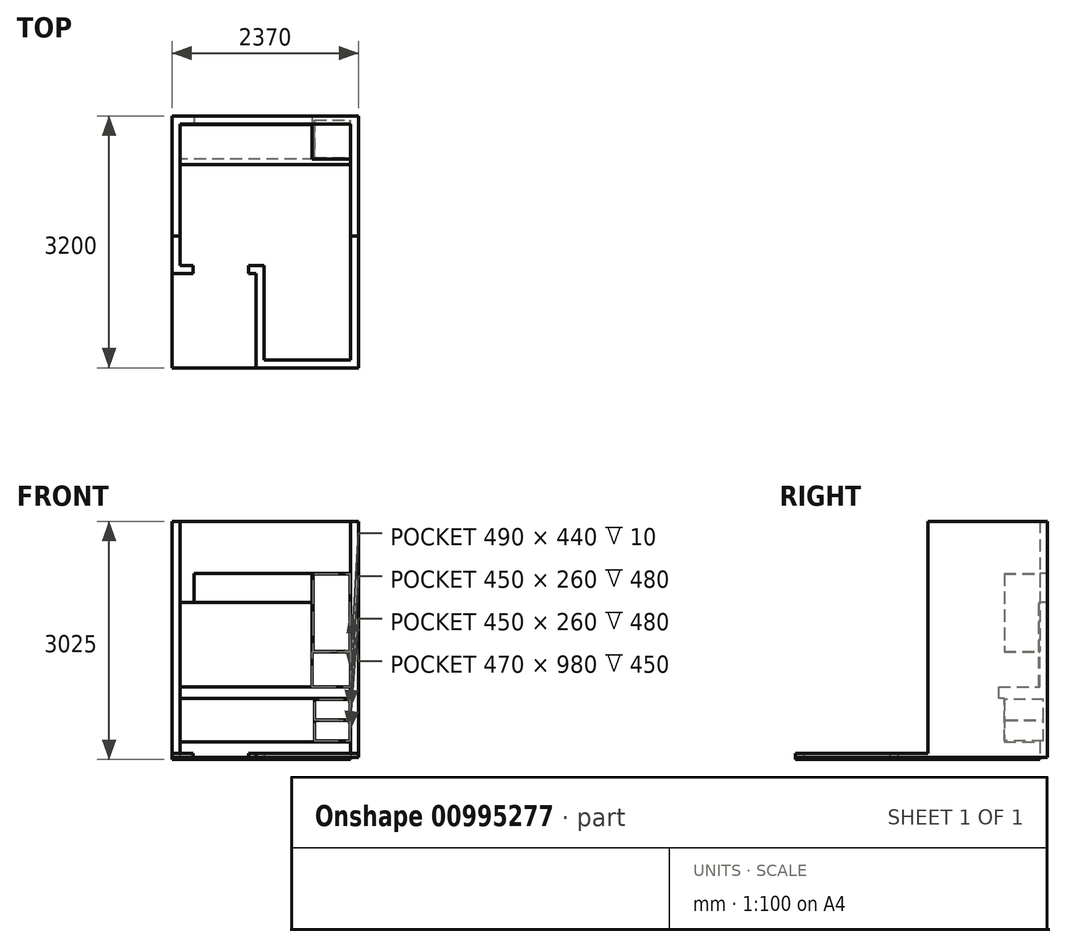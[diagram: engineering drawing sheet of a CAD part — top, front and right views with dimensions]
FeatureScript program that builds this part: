
annotation { "Feature Type Name" : "Feature", "Feature Type Description" : "" }
export const myFeature = defineFeature(function(context is Context, id is Id, definition is map)
    precondition{}
    {
        {
            var Q0;
            Q0=qCreatedBy(makeId("Top.planeOp"),FACE);
            var sketch = newSketch(context, id + "F0", { "sketchPlane" : qUnion([Q0])});
            skLineSegment(sketch, "E0", {"start": v(0, 0) * mm, "end": v(0, 1800) * mm});
            skLineSegment(sketch, "E1", {"start": v(0, 1800) * mm, "end": v(2170, 1800) * mm});
            skLineSegment(sketch, "E2", {"start": v(2170, 1800) * mm, "end": v(2170, -1200) * mm});
            skLineSegment(sketch, "E3", {"start": v(2170, -1200) * mm, "end": v(1070, -1200) * mm});
            skLineSegment(sketch, "E4", {"start": v(1070, -1200) * mm, "end": v(1070, 0) * mm});
            skLineSegment(sketch, "E5", {"start": v(1070, 0) * mm, "end": v(0, 0) * mm});
            skLineSegment(sketch, "E6.0", {"start": v(-100, 1900) * mm, "end": v(2270, 1900) * mm});
            skLineSegment(sketch, "E7.0", {"start": v(2270, 1900) * mm, "end": v(2270, -1300) * mm});
            skLineSegment(sketch, "E8.0", {"start": v(-100, -100) * mm, "end": v(-100, 1900) * mm});
            skLineSegment(sketch, "E8.1", {"start": v(970, -100) * mm, "end": v(-100, -100) * mm});
            skLineSegment(sketch, "E8.2", {"start": v(970, -1300) * mm, "end": v(970, -100) * mm});
            skLineSegment(sketch, "E8.3", {"start": v(2270, -1300) * mm, "end": v(970, -1300) * mm});
            skSolve(sketch);
        }
        {
            var Q0;
            Q0 = qSketchRegion(id + "F0", true);
            extrude(context, id + "F1", {"entities" : qUnion([Q0]), "depth" : 3000 * mm, "offsetDistance" : 25 * mm});
        }
        {
            var Q0;
            Q0=makeQuery(id+"F1.opExtrude","SWEPT_FACE",FACE,{"disambiguationData":[OSD([sQuery(id+"F0.wireOp",EDGE,"E8.1")])]});
            var sketch = newSketch(context, id + "F2", { "sketchPlane" : qUnion([Q0])});
            skLineSegment(sketch, "E9.bottom", {"start": v(170, 0) * mm, "end": v(870, 0) * mm});
            skLineSegment(sketch, "E9.top", {"start": v(170, 2100) * mm, "end": v(870, 2100) * mm});
            skLineSegment(sketch, "E9.left", {"start": v(170, 0) * mm, "end": v(170, 2100) * mm});
            skLineSegment(sketch, "E9.right", {"start": v(870, 0) * mm, "end": v(870, 2100) * mm});
            skSolve(sketch);
        }
        {
            var Q0;
            Q0=makeQuery(id+"F2.imprint","IMPRINT",FACE,{"disambiguationData":[TD([[makeQuery(id+"F2.imprint","IMPRINT",EDGE,{"derivedFrom":sQuery(id+"F2.wireOp",EDGE,"E9.bottom")}),-1.0]])]});
            extrude(context, id + "F3", {"entities" : qUnion([Q0]), "operationType" : NewBodyOperationType.REMOVE, "endBound" : BoundingType.UP_TO_NEXT, "oppositeDirection" : true, "depth" : 25 * mm, "offsetDistance" : 25 * mm});
        }
        {
            var Q0;
            Q0=makeQuery(id+"F1.opExtrude","SWEPT_FACE",FACE,{"disambiguationData":[OSD([sQuery(id+"F0.wireOp",EDGE,"E1")])]});
            var sketch = newSketch(context, id + "F4", { "sketchPlane" : qUnion([Q0])});
            skLineSegment(sketch, "E10.bottom", {"start": v(180, 2340) * mm, "end": v(1680, 2340) * mm});
            skLineSegment(sketch, "E10.top", {"start": v(180, 1970) * mm, "end": v(1680, 1970) * mm});
            skLineSegment(sketch, "E10.left", {"start": v(180, 2340) * mm, "end": v(180, 1970) * mm});
            skLineSegment(sketch, "E10.right", {"start": v(1680, 2340) * mm, "end": v(1680, 1970) * mm});
            skSolve(sketch);
        }
        {
            var Q0;
            Q0=makeQuery(id+"F4.imprint","IMPRINT",FACE,{"disambiguationData":[TD([[makeQuery(id+"F4.imprint","IMPRINT",EDGE,{"derivedFrom":sQuery(id+"F4.wireOp",EDGE,"E10.bottom")}),-1.0]])]});
            extrude(context, id + "F5", {"entities" : qUnion([Q0]), "operationType" : NewBodyOperationType.REMOVE, "endBound" : BoundingType.UP_TO_NEXT, "oppositeDirection" : true, "depth" : 25 * mm, "offsetDistance" : 25 * mm});
        }
        {
            var Q0;
            Q0=makeQuery(id+"F1.opExtrude","CAP_FACE",FACE,{"disambiguationData":[OSD([sQuery(id+"F0.wireOp",EDGE,"E0"),sQuery(id+"F0.wireOp",EDGE,"E1"),sQuery(id+"F0.wireOp",EDGE,"E2"),sQuery(id+"F0.wireOp",EDGE,"E3"),sQuery(id+"F0.wireOp",EDGE,"E4"),sQuery(id+"F0.wireOp",EDGE,"E5"),sQuery(id+"F0.wireOp",EDGE,"E6.0"),sQuery(id+"F0.wireOp",EDGE,"E7.0"),sQuery(id+"F0.wireOp",EDGE,"E8.0"),sQuery(id+"F0.wireOp",EDGE,"E8.1"),sQuery(id+"F0.wireOp",EDGE,"E8.2"),sQuery(id+"F0.wireOp",EDGE,"E8.3")])],"isStart":true});
            var sketch = newSketch(context, id + "F6", { "sketchPlane" : qUnion([Q0])});
            skLineSegment(sketch, "E11.bottom", {"start": v(-100, -1900) * mm, "end": v(2270, -1900) * mm});
            skLineSegment(sketch, "E11.top", {"start": v(-100, 1300) * mm, "end": v(2270, 1300) * mm});
            skLineSegment(sketch, "E11.left", {"start": v(-100, -1900) * mm, "end": v(-100, 1300) * mm});
            skLineSegment(sketch, "E11.right", {"start": v(2270, -1900) * mm, "end": v(2270, 1300) * mm});
            skSolve(sketch);
        }
        {
            var Q0;
            {var subQ12=sQuery(id+"F0.wireOp",EDGE,"E0");Q0=makeQuery(id+"F6.imprint","IMPRINT",FACE,{"disambiguationData":[TD([[makeQuery(id+"F6.imprint","IMPRINT",EDGE,{"derivedFrom":makeQuery(id+"F1.opExtrude","CAP_EDGE",EDGE,{"disambiguationData":[OSD([subQ12])],"isStart":true})}),1.0]])]});}
            extrude(context, id + "F7", {"entities" : qUnion([Q0]), "depth" : 25 * mm, "offsetDistance" : 25 * mm});
        }
        {
            var Q0;
            Q0=makeQuery(id+"F1.opExtrude","CAP_FACE",FACE,{"disambiguationData":[OSD([sQuery(id+"F0.wireOp",EDGE,"E0"),sQuery(id+"F0.wireOp",EDGE,"E1"),sQuery(id+"F0.wireOp",EDGE,"E2"),sQuery(id+"F0.wireOp",EDGE,"E3"),sQuery(id+"F0.wireOp",EDGE,"E4"),sQuery(id+"F0.wireOp",EDGE,"E5"),sQuery(id+"F0.wireOp",EDGE,"E6.0"),sQuery(id+"F0.wireOp",EDGE,"E7.0"),sQuery(id+"F0.wireOp",EDGE,"E8.0"),sQuery(id+"F0.wireOp",EDGE,"E8.1"),sQuery(id+"F0.wireOp",EDGE,"E8.2"),sQuery(id+"F0.wireOp",EDGE,"E8.3")])],"isStart":false});
            var sketch = newSketch(context, id + "F8", { "sketchPlane" : qUnion([Q0])});
            skLineSegment(sketch, "E12.bottom", {"start": v(2466.68, -1550.03) * mm, "end": v(-472.08, -1550.03) * mm});
            skLineSegment(sketch, "E12.top", {"start": v(2466.68, 377.63) * mm, "end": v(-472.08, 377.63) * mm});
            skLineSegment(sketch, "E12.left", {"start": v(2466.68, -1550.03) * mm, "end": v(2466.68, 377.63) * mm});
            skLineSegment(sketch, "E12.right", {"start": v(-472.08, -1550.03) * mm, "end": v(-472.08, 377.63) * mm});
            skSolve(sketch);
        }
        {
            var Q0;
            Q0=makeQuery(id+"F8.imprint","IMPRINT",FACE,{"disambiguationData":[TD([[makeQuery(id+"F8.imprint","IMPRINT",EDGE,{"derivedFrom":sQuery(id+"F8.wireOp",EDGE,"E12.bottom")}),-1.0]])]});
            var Q1;
            {var subQ1=makeQuery(id+"F1.opExtrude","CAP_EDGE",EDGE,{"disambiguationData":[OSD([sQuery(id+"F0.wireOp",EDGE,"E3")])],"isStart":false});Q1=makeQuery(id+"F8.imprint","IMPRINT",FACE,{"disambiguationData":[TD([[makeQuery(id+"F8.imprint","IMPRINT",EDGE,{"derivedFrom":subQ1}),-1.0]])]});}
            var Q2;
            {var subQ0=makeQuery(id+"F1.opExtrude","CAP_EDGE",EDGE,{"disambiguationData":[OSD([sQuery(id+"F0.wireOp",EDGE,"E3")])],"isStart":false});Q2=makeQuery(id+"F8.imprint","IMPRINT",FACE,{"disambiguationData":[TD([[makeQuery(id+"F8.imprint","IMPRINT",EDGE,{"derivedFrom":subQ0}),1.0]])]});}
            extrude(context, id + "F9", {"entities" : qUnion([Q0, Q1, Q2]), "operationType" : NewBodyOperationType.REMOVE, "oppositeDirection" : true, "depth" : 2950 * mm, "offsetDistance" : 25 * mm});
        }
        {
            var Q0;
            Q0=makeQuery(id+"F1.opExtrude","SWEPT_FACE",FACE,{"disambiguationData":[OSD([sQuery(id+"F0.wireOp",EDGE,"E1")])]});
            var sketch = newSketch(context, id + "F10", { "sketchPlane" : qUnion([Q0])});
            skLineSegment(sketch, "E13.bottom", {"start": v(2170, 900) * mm, "end": v(0, 900) * mm});
            skLineSegment(sketch, "E13.top", {"start": v(2170, 200) * mm, "end": v(0, 200) * mm});
            skLineSegment(sketch, "E13.left", {"start": v(2170, 900) * mm, "end": v(2170, 200) * mm});
            skLineSegment(sketch, "E13.right", {"start": v(0, 900) * mm, "end": v(0, 200) * mm});
            skSolve(sketch);
        }
        {
            var Q0;
            Q0=makeQuery(id+"F10.imprint","IMPRINT",FACE,{"disambiguationData":[TD([[makeQuery(id+"F10.imprint","IMPRINT",EDGE,{"derivedFrom":sQuery(id+"F10.wireOp",EDGE,"E13.bottom")}),1.0]])]});
            extrude(context, id + "F11", {"entities" : qUnion([Q0]), "operationType" : NewBodyOperationType.ADD, "depth" : 450 * mm, "offsetDistance" : 25 * mm});
        }
        {
            var Q0;
            Q0=makeQuery(id+"F11.opExtrude","SWEPT_FACE",FACE,{"disambiguationData":[OSD([sQuery(id+"F10.wireOp",EDGE,"E13.bottom")])]});
            var sketch = newSketch(context, id + "F12", { "sketchPlane" : qUnion([Q0])});
            skLineSegment(sketch, "E14.bottom", {"start": v(0, 1800) * mm, "end": v(2170, 1800) * mm});
            skLineSegment(sketch, "E14.top", {"start": v(0, 1280) * mm, "end": v(2170, 1280) * mm});
            skLineSegment(sketch, "E14.left", {"start": v(0, 1800) * mm, "end": v(0, 1280) * mm});
            skLineSegment(sketch, "E14.right", {"start": v(2170, 1800) * mm, "end": v(2170, 1280) * mm});
            skSolve(sketch);
        }
        {
            var Q0;
            {var subQ0=sQuery(id+"F12.wireOp",EDGE,"E14.top");Q0=makeQuery(id+"F12.imprint","IMPRINT",FACE,{"disambiguationData":[TD([[makeQuery(id+"F12.imprint","IMPRINT",EDGE,{"derivedFrom":subQ0}),1.0]])]});}
            var Q1;
            {var subQ0=sQuery(id+"F12.wireOp",EDGE,"E14.bottom");Q1=makeQuery(id+"F12.imprint","IMPRINT",FACE,{"disambiguationData":[TD([[makeQuery(id+"F12.imprint","IMPRINT",EDGE,{"derivedFrom":subQ0}),1.0]])]});}
            extrude(context, id + "F13", {"entities" : qUnion([Q0, Q1]), "operationType" : NewBodyOperationType.ADD, "oppositeDirection" : true, "depth" : 150 * mm, "offsetDistance" : 25 * mm});
        }
        {
            var Q0;
            {var subQ1=sQuery(id+"F0.wireOp",EDGE,"E1");Q0=makeQuery(id+"F11.boolean.opBoolean","SPLIT",FACE,{"disambiguationData":[TD([makeQuery(id+"F5.boolean.opBoolean","COPY",FACE,{"derivedFrom":makeQuery(id+"F5.opExtrude","SWEPT_FACE",FACE,{"disambiguationData":[OSD([sQuery(id+"F4.wireOp",EDGE,"E10.bottom")])]})})])],"derivedFrom":makeQuery(id+"F1.opExtrude","SWEPT_FACE",FACE,{"disambiguationData":[OSD([subQ1])]})});}
            var sketch = newSketch(context, id + "F14", { "sketchPlane" : qUnion([Q0])});
            skLineSegment(sketch, "E15.bottom", {"start": v(0, 900) * mm, "end": v(1680, 900) * mm});
            skLineSegment(sketch, "E15.top", {"start": v(0, 1970) * mm, "end": v(1680, 1970) * mm});
            skLineSegment(sketch, "E15.left", {"start": v(0, 900) * mm, "end": v(0, 1970) * mm});
            skLineSegment(sketch, "E15.right", {"start": v(1680, 900) * mm, "end": v(1680, 1970) * mm});
            skSolve(sketch);
        }
        {
            var Q0;
            Q0 = qSketchRegion(id + "F14", true);
            extrude(context, id + "F15", {"entities" : qUnion([Q0]), "operationType" : NewBodyOperationType.ADD, "depth" : 10 * mm, "offsetDistance" : 25 * mm});
        }
        {
            var Q0;
            Q0=makeQuery(id+"F1.opExtrude","SWEPT_FACE",FACE,{"disambiguationData":[OSD([sQuery(id+"F0.wireOp",EDGE,"E2")])]});
            var sketch = newSketch(context, id + "F16", { "sketchPlane" : qUnion([Q0])});
            skLineSegment(sketch, "E16", {"start": v(-800, 0) * mm, "end": v(-800, 1586.75) * mm});
            skSolve(sketch);
        }
        {
            var Q0;
            Q0=makeQuery(id+"F11.opExtrude","CAP_FACE",FACE,{"disambiguationData":[OSD([sQuery(id+"F10.wireOp",EDGE,"E13.bottom"),sQuery(id+"F10.wireOp",EDGE,"E13.top"),sQuery(id+"F10.wireOp",EDGE,"E13.left"),sQuery(id+"F10.wireOp",EDGE,"E13.right")])],"isStart":false});
            var sketch = newSketch(context, id + "F17", { "sketchPlane" : qUnion([Q0])});
            skLineSegment(sketch, "E17.bottom", {"start": v(10, 210) * mm, "end": v(510, 210) * mm});
            skLineSegment(sketch, "E17.top", {"start": v(10, 740) * mm, "end": v(510, 740) * mm});
            skLineSegment(sketch, "E17.left", {"start": v(10, 210) * mm, "end": v(10, 740) * mm});
            skLineSegment(sketch, "E17.right", {"start": v(510, 210) * mm, "end": v(510, 740) * mm});
            skLineSegment(sketch, "E18.1.0.0", {"start": v(2160, 210) * mm, "end": v(2160, 740) * mm});
            skLineSegment(sketch, "E18.1.0.1", {"start": v(1710, 210) * mm, "end": v(1710, 740) * mm});
            skLineSegment(sketch, "E18.1.0.2", {"start": v(1710, 740) * mm, "end": v(2160, 740) * mm});
            skLineSegment(sketch, "E18.1.0.3", {"start": v(1710, 210) * mm, "end": v(2160, 210) * mm});
            skLineSegment(sketch, "E18.direction1", {"start": v(10, 210) * mm, "end": v(1710, 210) * mm, "construction": true});
            skSolve(sketch);
        }
        {
            var Q0;
            Q0=makeQuery(id+"F17.imprint","IMPRINT",FACE,{"disambiguationData":[TD([[makeQuery(id+"F17.imprint","IMPRINT",EDGE,{"derivedFrom":sQuery(id+"F17.wireOp",EDGE,"E18.1.0.0")}),1.0]])]});
            extrude(context, id + "F18", {"entities" : qUnion([Q0]), "operationType" : NewBodyOperationType.REMOVE, "oppositeDirection" : true, "depth" : 500 * mm, "offsetDistance" : 25 * mm});
        }
        {
            var Q0;
            Q0=makeQuery(id+"F18.boolean.opBoolean","COPY",FACE,{"derivedFrom":makeQuery(id+"F18.opExtrude","CAP_FACE",FACE,{"disambiguationData":[OSD([sQuery(id+"F17.wireOp",EDGE,"E18.1.0.0"),sQuery(id+"F17.wireOp",EDGE,"E18.1.0.1"),sQuery(id+"F17.wireOp",EDGE,"E18.1.0.2"),sQuery(id+"F17.wireOp",EDGE,"E18.1.0.3")])],"isStart":false})});
            var sketch = newSketch(context, id + "F19", { "sketchPlane" : qUnion([Q0])});
            skLineSegment(sketch, "E19.bottom", {"start": v(1710, 480) * mm, "end": v(2160, 480) * mm});
            skLineSegment(sketch, "E19.top", {"start": v(1710, 470) * mm, "end": v(2160, 470) * mm});
            skLineSegment(sketch, "E19.left", {"start": v(1710, 480) * mm, "end": v(1710, 470) * mm});
            skLineSegment(sketch, "E19.right", {"start": v(2160, 480) * mm, "end": v(2160, 470) * mm});
            skSolve(sketch);
        }
        {
            var Q0;
            Q0=makeQuery(id+"F19.imprint","IMPRINT",FACE,{"disambiguationData":[TD([[makeQuery(id+"F19.imprint","IMPRINT",EDGE,{"derivedFrom":sQuery(id+"F19.wireOp",EDGE,"E19.bottom")}),-1.0]])]});
            extrude(context, id + "F20", {"entities" : qUnion([Q0]), "operationType" : NewBodyOperationType.ADD, "depth" : 480 * mm, "offsetDistance" : 25 * mm});
        }
        {
            var Q0;
            {var subQ1=sQuery(id+"F0.wireOp",EDGE,"E1");Q0=makeQuery(id+"F11.boolean.opBoolean","SPLIT",FACE,{"disambiguationData":[TD([makeQuery(id+"F5.boolean.opBoolean","COPY",FACE,{"derivedFrom":makeQuery(id+"F5.opExtrude","SWEPT_FACE",FACE,{"disambiguationData":[OSD([sQuery(id+"F4.wireOp",EDGE,"E10.bottom")])]})})])],"derivedFrom":makeQuery(id+"F1.opExtrude","SWEPT_FACE",FACE,{"disambiguationData":[OSD([subQ1])]})});}
            var sketch = newSketch(context, id + "F21", { "sketchPlane" : qUnion([Q0])});
            skLineSegment(sketch, "E20.bottom", {"start": v(1680, 2340) * mm, "end": v(2170, 2340) * mm});
            skLineSegment(sketch, "E20.top", {"start": v(1680, 1340) * mm, "end": v(2170, 1340) * mm});
            skLineSegment(sketch, "E20.left", {"start": v(1680, 2340) * mm, "end": v(1680, 1340) * mm});
            skLineSegment(sketch, "E20.right", {"start": v(2170, 2340) * mm, "end": v(2170, 1340) * mm});
            skLineSegment(sketch, "E21.0", {"start": v(1690, 2330) * mm, "end": v(2160, 2330) * mm});
            skLineSegment(sketch, "E21.1", {"start": v(1690, 2330) * mm, "end": v(1690, 1350) * mm});
            skLineSegment(sketch, "E21.2", {"start": v(1690, 1350) * mm, "end": v(2160, 1350) * mm});
            skLineSegment(sketch, "E21.3", {"start": v(2160, 2330) * mm, "end": v(2160, 1350) * mm});
            skLineSegment(sketch, "E22.0", {"start": v(2175, 3005) * mm, "end": v(-5, 3005) * mm});
            skLineSegment(sketch, "E22.1", {"start": v(2175, 895) * mm, "end": v(2175, 3005) * mm});
            skLineSegment(sketch, "E22.2", {"start": v(-5, 3005) * mm, "end": v(-5, 1965) * mm});
            skLineSegment(sketch, "E22.3", {"start": v(1675, 895) * mm, "end": v(2175, 895) * mm});
            skLineSegment(sketch, "E22.4", {"start": v(1675, 1970) * mm, "end": v(1675, 895) * mm});
            skLineSegment(sketch, "E22.5", {"start": v(-5, 1965) * mm, "end": v(185, 1965) * mm});
            skLineSegment(sketch, "E22.6", {"start": v(185, 1965) * mm, "end": v(185, 2335) * mm});
            skLineSegment(sketch, "E22.7", {"start": v(185, 2335) * mm, "end": v(1675, 2335) * mm});
            skLineSegment(sketch, "E22.8", {"start": v(1675, 2335) * mm, "end": v(1675, 1970) * mm});
            skSolve(sketch);
        }
        {
            var Q0;
            {var subQ3=sQuery(id+"F21.wireOp",EDGE,"E20.bottom");Q0=makeQuery(id+"F21.imprint","IMPRINT",FACE,{"disambiguationData":[TD([[makeQuery(id+"F21.imprint","IMPRINT",EDGE,{"derivedFrom":subQ3}),-1.0]])]});}
            extrude(context, id + "F22", {"entities" : qUnion([Q0]), "operationType" : NewBodyOperationType.ADD, "depth" : 450 * mm, "offsetDistance" : 25 * mm});
        }
    });
